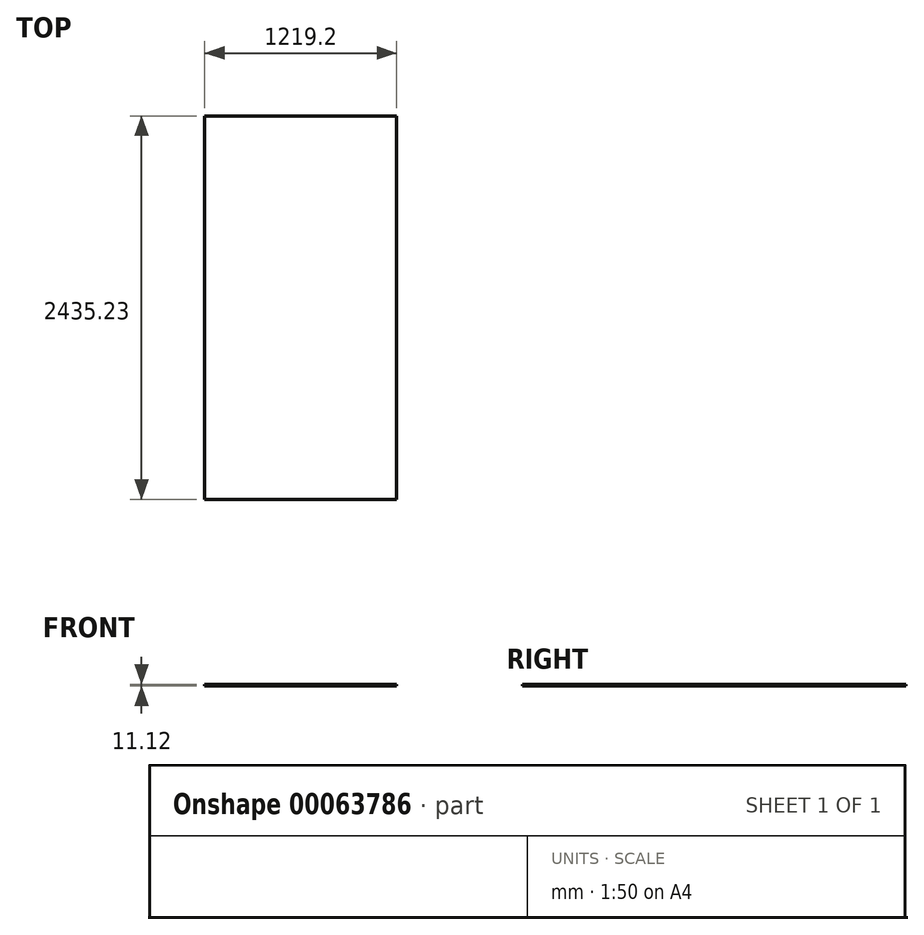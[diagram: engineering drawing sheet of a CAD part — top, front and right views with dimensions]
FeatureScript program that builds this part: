
annotation { "Feature Type Name" : "Feature", "Feature Type Description" : "" }
export const myFeature = defineFeature(function(context is Context, id is Id, definition is map)
    precondition{}
    {
        {
            var Q0;
            Q0=qCreatedBy(makeId("Top.planeOp"),FACE);
            var sketch = newSketch(context, id + "F0", { "sketchPlane" : qUnion([Q0])});
            skLineSegment(sketch, "E0.bottom", {"start": v(-609.6, 1911.45) * mm, "end": v(609.6, 1911.45) * mm});
            skLineSegment(sketch, "E0.top", {"start": v(-609.6, -523.78) * mm, "end": v(609.6, -523.78) * mm});
            skLineSegment(sketch, "E0.left", {"start": v(-609.6, 1911.45) * mm, "end": v(-609.6, -523.78) * mm});
            skLineSegment(sketch, "E0.right", {"start": v(609.6, 1911.45) * mm, "end": v(609.6, -523.78) * mm});
            skSolve(sketch);
        }
        {
            var Q0;
            Q0 = qSketchRegion(id + "F0", true);
            extrude(context, id + "F1", {"entities" : qUnion([Q0]), "endBound" : BoundingType.SYMMETRIC, "depth" : 11.1 * mm});
        }
    });
